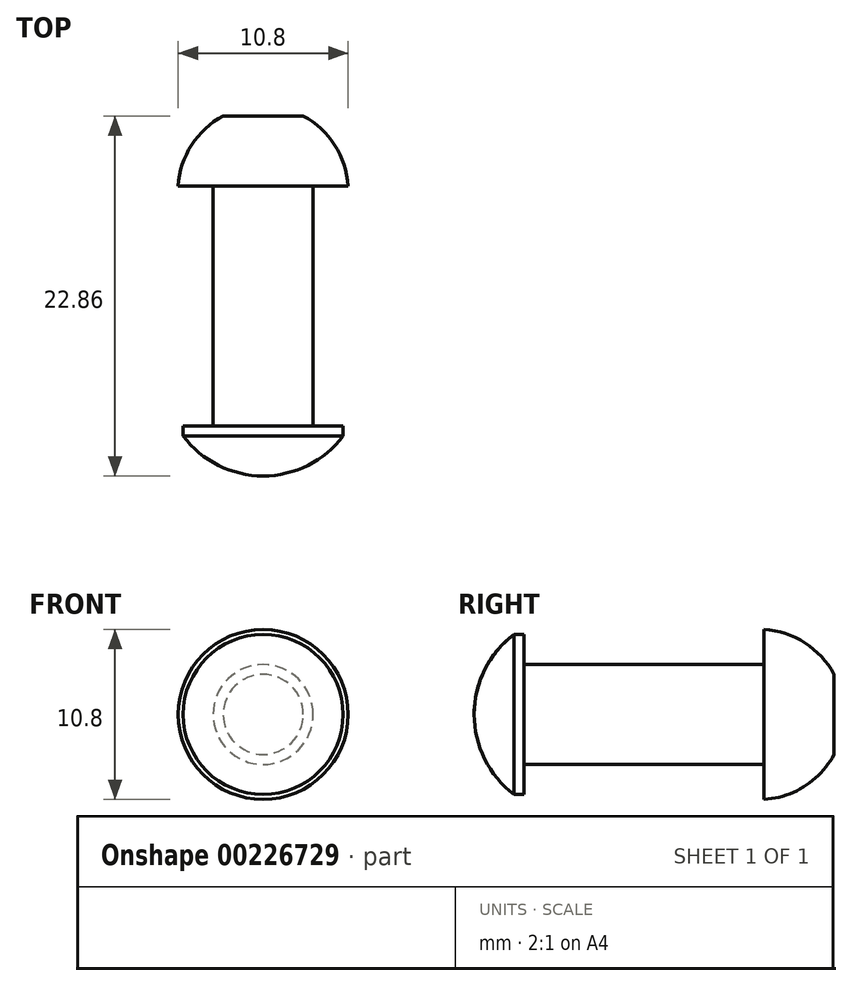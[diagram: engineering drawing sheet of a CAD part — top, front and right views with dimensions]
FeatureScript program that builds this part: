
annotation { "Feature Type Name" : "Feature", "Feature Type Description" : "" }
export const myFeature = defineFeature(function(context is Context, id is Id, definition is map)
    precondition{}
    {
        {
            var Q0;
            Q0=qCreatedBy(makeId("Right.planeOp"),FACE);
            var sketch = newSketch(context, id + "F0", { "sketchPlane" : qUnion([Q0])});
            skLineSegment(sketch, "E0", {"start": v(-4.44, 5.4) * mm, "end": v(-4.44, 3.18) * mm});
            skLineSegment(sketch, "E1", {"start": v(-4.44, 3.18) * mm, "end": v(-19.69, 3.17) * mm});
            skLineSegment(sketch, "E2", {"start": v(-19.69, 3.17) * mm, "end": v(-19.69, 5.08) * mm});
            skLineSegment(sketch, "E3", {"start": v(-19.69, 5.08) * mm, "end": v(-20.32, 5.08) * mm});
            skLineSegment(sketch, "E4", {"start": v(0, 0) * mm, "end": v(-22.86, 0) * mm, "construction": true});
            skArc(sketch, "E5", {"start": v(-20.32, 5.08) * mm, "mid": v(-22.19, 2.84) * mm, "end": v(-22.86, 0) * mm});
            skLineSegment(sketch, "E6", {"start": v(0, 0) * mm, "end": v(0, 2.54) * mm});
            skArc(sketch, "E7", {"start": v(0, 2.54) * mm, "mid": v(-1.85, 4.55) * mm, "end": v(-4.45, 5.4) * mm});
            skLineSegment(sketch, "E8", {"start": v(-22.86, 0) * mm, "end": v(0, 0) * mm});
            skSolve(sketch);
        }
        {
            var Q0;
            Q0 = qSketchRegion(id + "F0", true);
            var Q1;
            Q1=sQuery(id+"F0.wireOp",EDGE,"E8");
            revolve(context, id + "F1", {"entities" : qUnion([Q0]), "axis" : qUnion([Q1]), "revolveType" : RevolveType.FULL});
        }
    });
